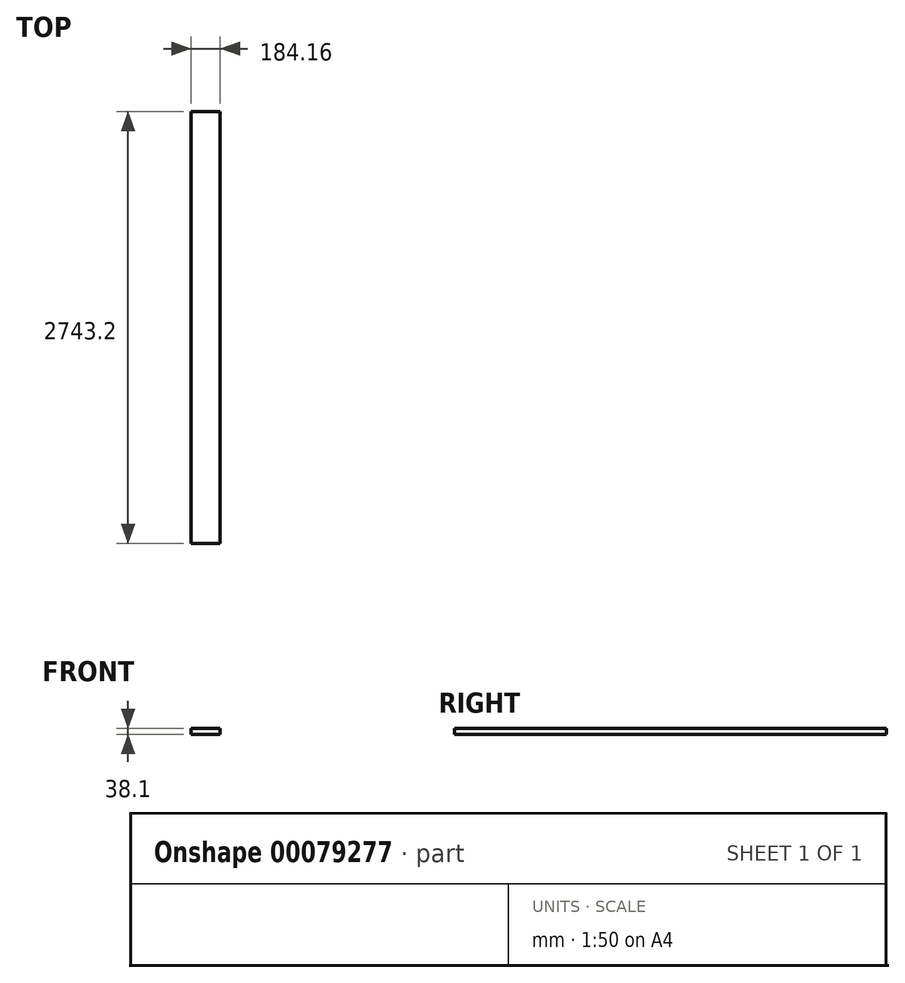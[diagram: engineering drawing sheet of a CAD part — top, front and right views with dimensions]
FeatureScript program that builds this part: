
annotation { "Feature Type Name" : "Feature", "Feature Type Description" : "" }
export const myFeature = defineFeature(function(context is Context, id is Id, definition is map)
    precondition{}
    {
        {
            var Q0;
            Q0=qCreatedBy(makeId("Front.planeOp"),FACE);
            var sketch = newSketch(context, id + "F0", { "sketchPlane" : qUnion([Q0])});
            skLineSegment(sketch, "E0.bottom", {"start": v(92.07, 19.05) * mm, "end": v(-92.08, 19.05) * mm});
            skLineSegment(sketch, "E0.top", {"start": v(92.07, -19.05) * mm, "end": v(-92.07, -19.05) * mm});
            skLineSegment(sketch, "E0.left", {"start": v(92.07, 19.05) * mm, "end": v(92.08, -19.05) * mm});
            skLineSegment(sketch, "E0.right", {"start": v(-92.08, 19.05) * mm, "end": v(-92.07, -19.05) * mm});
            skPoint(sketch, "E0.middle", {"position": v(0, 0) * mm});
            skSolve(sketch);
        }
        {
            var Q0;
            Q0 = qSketchRegion(id + "F0", true);
            extrude(context, id + "F1", {"entities" : qUnion([Q0]), "endBound" : BoundingType.SYMMETRIC, "depth" : 2743.2 * mm});
        }
    });
